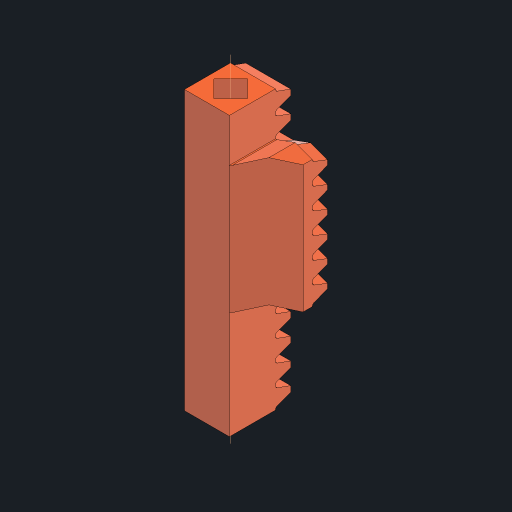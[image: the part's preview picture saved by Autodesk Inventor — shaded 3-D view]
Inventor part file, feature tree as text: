
AUTODESK INVENTOR PART (.ipt)
format: ipt  version: 2023.2 (Build 272271030, 271C)  size: 709,632 bytes
history: native  units: mm
features: sketch x6, projected_geometry x5, extrude x4, sweep x1, pattern_linear x1, other x1, chamfer x1
ambient origin geometry x8: Origin, YZ Plane, XZ Plane, XY Plane, X Axis, Y Axis, Z Axis, Center Point
bodies: Solid1 (feature_tree)
feature tree (19):
  extrude  "Extrusion1"  Depth=40.840704mm
  sweep  "Sweep1"
  pattern_linear  "Rectangular Pattern1"  Spacing1=7.0mm  [1 undecoded]
  sketch  "Sketch4"  dims[d6=1.570796mm]
  extrude  "Extrusion7"  Depth=5.4mm
  extrude  "Extrusion8"  Depth=5.4mm
  extrude  "Extrusion9"  TaperAngle=0.0deg  [1 undecoded]
  other  "Work Axis1"
  chamfer  "Chamfer2"  Distance=140.0mm
  sketch  "Sketch1"  dims[d0=12.0mm d1=40.840704mm]
  sketch  "Sketch2"  dims[d2=9.0mm d3=0.0mm d4=1.0mm]
  projected_geometry  "Projected Loop1"
  sketch  "Sketch3"  dims[d5=1.25mm]
  projected_geometry  "Projected Loop2"
  sketch  "Sketch8"  dims[d7=12.217305mm]
  projected_geometry  "Projected Loop21"
  sketch  "Sketch9"  dims[d17=0.38mm d27=7.0mm d28=5.0mm d29=3.490659mm d30=0.0mm d31=0.0mm d32=140.0mm d34=3.141593mm d49=10.0mm d50=0.0mm d56=0.0mm d57=0.0mm d58=0.0mm d59=0.0mm d60=3.5mm d61=3.3mm d62=5.5mm d63=6.6mm d64=5.4mm d65=2.0mm d66=45.0deg d43=0.5mm d44=0.872665mm d45=0.5mm d46=0.872665mm]
  projected_geometry  "Projected Loop22"
  projected_geometry  "Projected Loop23"
note: 2 required parameter values undecoded (feature->parameter linkage not recoverable at this tier; creation-order binding heuristic only, values carry confidence <= 0.55)
